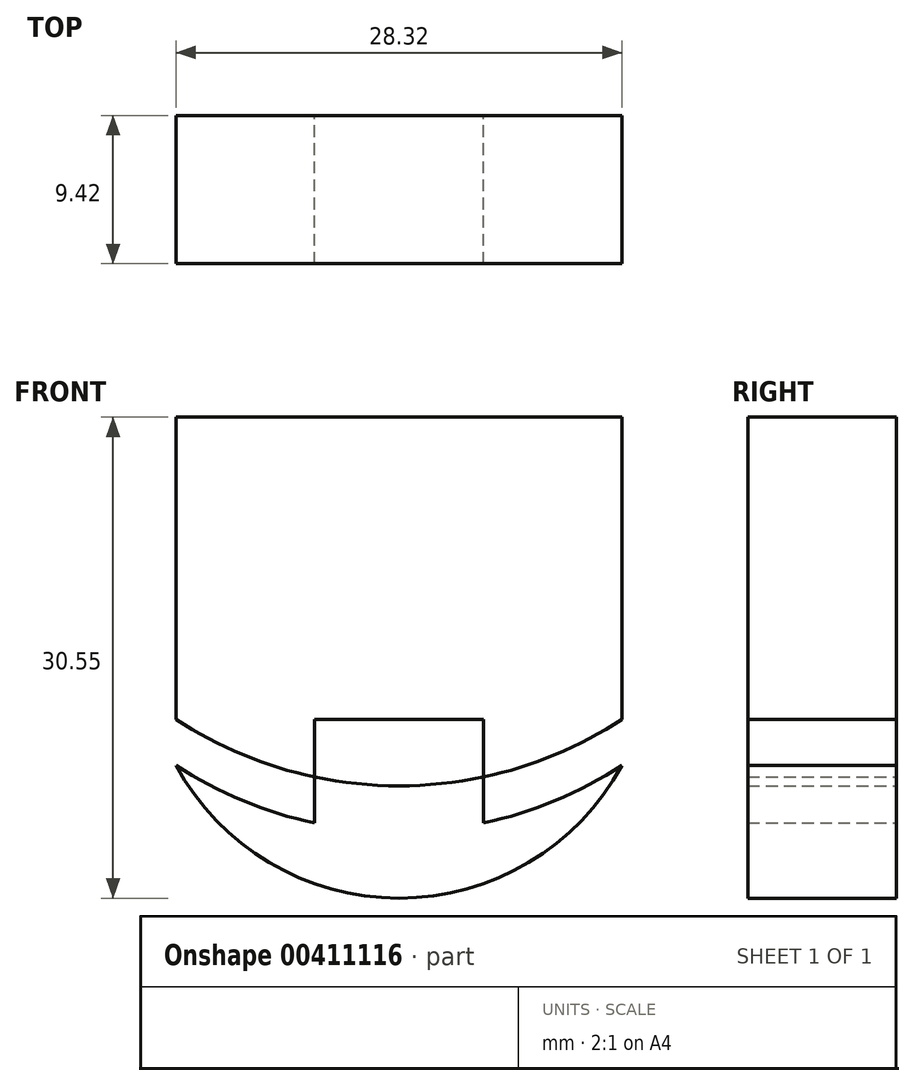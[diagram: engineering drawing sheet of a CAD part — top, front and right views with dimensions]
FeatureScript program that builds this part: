
annotation { "Feature Type Name" : "Feature", "Feature Type Description" : "" }
export const myFeature = defineFeature(function(context is Context, id is Id, definition is map)
    precondition{}
    {
        {
            var Q0;
            Q0=qCreatedBy(makeId("Front.planeOp"),FACE);
            var sketch = newSketch(context, id + "F0", { "sketchPlane" : qUnion([Q0])});
            skLineSegment(sketch, "E0.bottom", {"start": v(0, 0) * mm, "end": v(28.32, 0) * mm});
            skLineSegment(sketch, "E0.top", {"start": v(0, 19.2) * mm, "end": v(28.32, 19.2) * mm});
            skLineSegment(sketch, "E0.left", {"start": v(0, 0) * mm, "end": v(0, 19.2) * mm});
            skLineSegment(sketch, "E0.right", {"start": v(28.32, 0) * mm, "end": v(28.32, 19.2) * mm});
            skArc(sketch, "E1", {"start": v(0, 0) * mm, "mid": v(14.16, -4.22) * mm, "end": v(28.32, 0) * mm});
            skPoint(sketch, "E2", {"position": v(14.16, -4.22) * mm});
            skLineSegment(sketch, "E3.bottom", {"start": v(8.8, 0) * mm, "end": v(19.52, 0) * mm});
            skLineSegment(sketch, "E3.top", {"start": v(8.8, -7.14) * mm, "end": v(19.52, -7.14) * mm});
            skLineSegment(sketch, "E3.left", {"start": v(8.8, 0) * mm, "end": v(8.8, -7.14) * mm});
            skLineSegment(sketch, "E3.right", {"start": v(19.52, 0) * mm, "end": v(19.52, -7.14) * mm});
            skLineSegment(sketch, "E4", {"start": v(14.16, -4.22) * mm, "end": v(8.8, -4.22) * mm, "construction": true});
            skLineSegment(sketch, "E5", {"start": v(14.16, -4.22) * mm, "end": v(19.52, -4.22) * mm, "construction": true});
            skArc(sketch, "E6", {"start": v(0, -2.92) * mm, "mid": v(14.16, -7.14) * mm, "end": v(28.32, -2.92) * mm});
            skArc(sketch, "E7", {"start": v(0, -2.92) * mm, "mid": v(14.16, -11.35) * mm, "end": v(28.32, -2.92) * mm});
            skLineSegment(sketch, "E8", {"start": v(0, -2.92) * mm, "end": v(28.32, -2.92) * mm, "construction": true});
            skPoint(sketch, "E9", {"position": v(14.16, -7.14) * mm});
            skPoint(sketch, "E10", {"position": v(14.16, -11.35) * mm});
            skSolve(sketch);
        }
        {
            var Q0;
            Q0=makeQuery(id+"F0.imprint","IMPRINT",FACE,{"disambiguationData":[TD([[makeQuery(id+"F0.imprint","IMPRINT",EDGE,{"derivedFrom":sQuery(id+"F0.wireOp",EDGE,"E0.top")}),-1.0]])]});
            var Q1;
            {var subQ0=sQuery(id+"F0.wireOp",EDGE,"E1");var subQ3=sQuery(id+"F0.wireOp",EDGE,"E3.left");var subQ5=makeQuery(id+"F0.imprint","INTERSECT",VERTEX,{"derivedFrom":[subQ0,subQ3]});Q1=makeQuery(id+"F0.imprint","IMPRINT",FACE,{"disambiguationData":[TD([[makeQuery(id+"F0.imprint","IMPRINT",EDGE,{"disambiguationData":[TD([[subQ5,1.0]])],"derivedFrom":subQ0}),1.0]])]});}
            var Q2;
            {var subQ5=sQuery(id+"F0.wireOp",EDGE,"E3.bottom");Q2=makeQuery(id+"F0.imprint","IMPRINT",FACE,{"disambiguationData":[TD([[makeQuery(id+"F0.imprint","IMPRINT",EDGE,{"derivedFrom":subQ5}),-1.0]])]});}
            var Q3;
            {var subQ0=sQuery(id+"F0.wireOp",EDGE,"E1");var subQ3=sQuery(id+"F0.wireOp",EDGE,"E3.right");var subQ5=makeQuery(id+"F0.imprint","INTERSECT",VERTEX,{"derivedFrom":[subQ0,subQ3]});Q3=makeQuery(id+"F0.imprint","IMPRINT",FACE,{"disambiguationData":[TD([[makeQuery(id+"F0.imprint","IMPRINT",EDGE,{"disambiguationData":[TD([[subQ5,-1.0]])],"derivedFrom":subQ0}),1.0]])]});}
            var Q4;
            {var subQ1=sQuery(id+"F0.wireOp",EDGE,"E3.left");var subQ5=sQuery(id+"F0.wireOp",EDGE,"E1");var subQ8=makeQuery(id+"F0.imprint","INTERSECT",VERTEX,{"derivedFrom":[subQ5,subQ1]});Q4=makeQuery(id+"F0.imprint","IMPRINT",FACE,{"disambiguationData":[TD([[makeQuery(id+"F0.imprint","IMPRINT",EDGE,{"disambiguationData":[TD([[subQ8,-1.0]])],"derivedFrom":subQ5}),-1.0]])]});}
            var Q5;
            {var subQ9=sQuery(id+"F0.wireOp",EDGE,"E7");Q5=makeQuery(id+"F0.imprint","IMPRINT",FACE,{"disambiguationData":[TD([[makeQuery(id+"F0.imprint","IMPRINT",EDGE,{"derivedFrom":subQ9}),1.0]])]});}
            var Q6;
            {var subQ0=sQuery(id+"F0.wireOp",EDGE,"E3.right");var subQ1=sQuery(id+"F0.wireOp",EDGE,"E3.top");var subQ2=makeQuery(id+"F0.imprint","INTERSECT",VERTEX,{"derivedFrom":[subQ1,subQ0]});Q6=makeQuery(id+"F0.imprint","IMPRINT",FACE,{"disambiguationData":[TD([[makeQuery(id+"F0.imprint","IMPRINT",EDGE,{"disambiguationData":[TD([[subQ2,1.0]])],"derivedFrom":subQ1}),1.0]])]});}
            var Q7;
            {var subQ0=sQuery(id+"F0.wireOp",EDGE,"E3.left");var subQ1=sQuery(id+"F0.wireOp",EDGE,"E3.top");var subQ2=makeQuery(id+"F0.imprint","INTERSECT",VERTEX,{"derivedFrom":[subQ1,subQ0]});Q7=makeQuery(id+"F0.imprint","IMPRINT",FACE,{"disambiguationData":[TD([[makeQuery(id+"F0.imprint","IMPRINT",EDGE,{"disambiguationData":[TD([[subQ2,-1.0]])],"derivedFrom":subQ1}),1.0]])]});}
            extrude(context, id + "F1", {"entities" : qUnion([Q0, Q1, Q2, Q3, Q4, Q5, Q6, Q7]), "depth" : 9.42 * mm});
        }
    });
